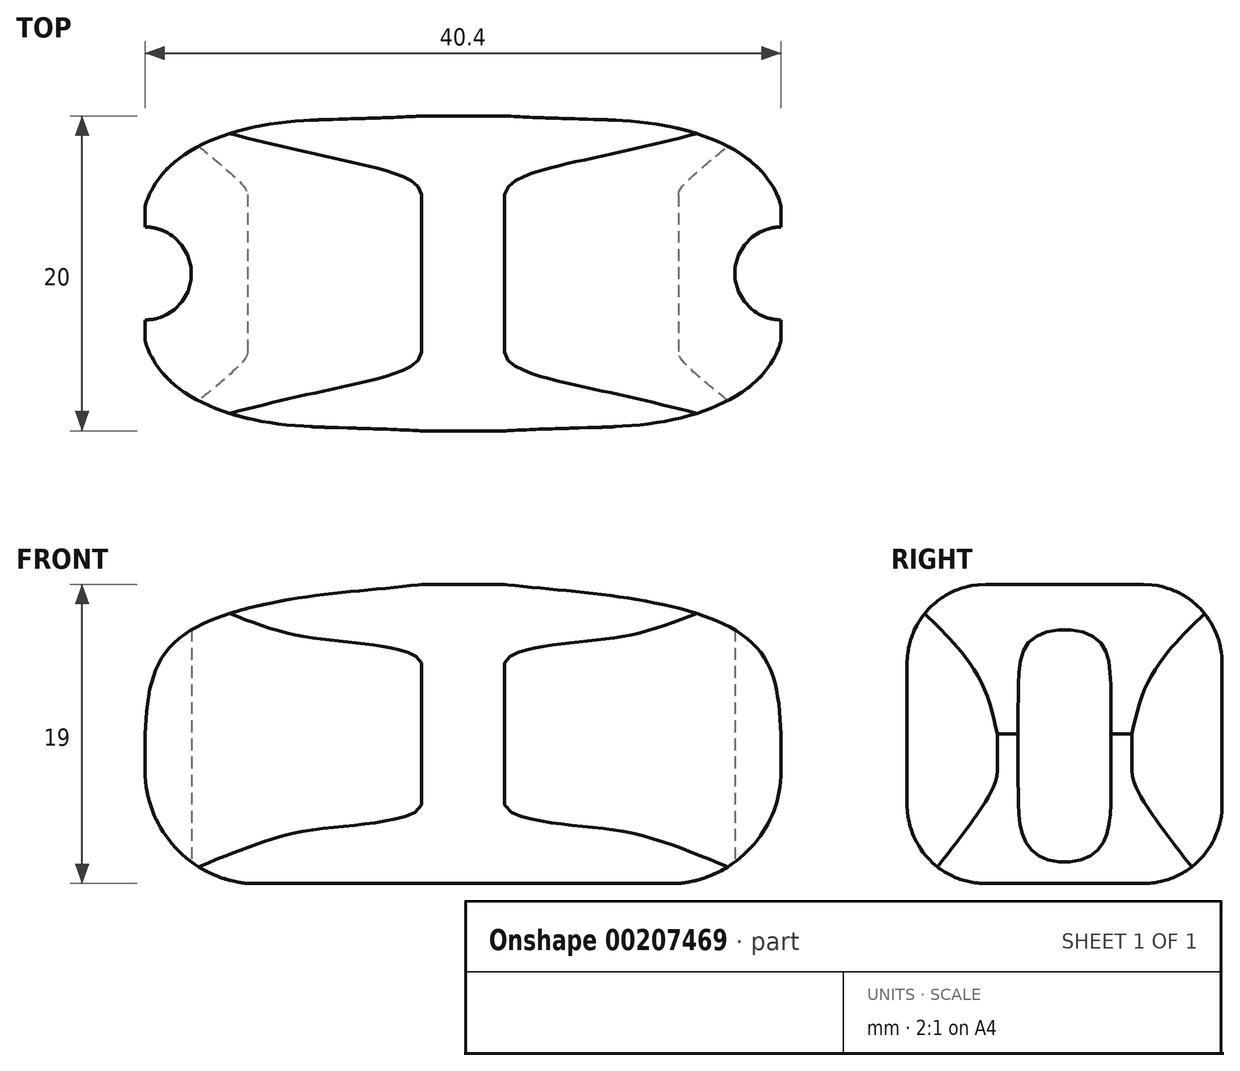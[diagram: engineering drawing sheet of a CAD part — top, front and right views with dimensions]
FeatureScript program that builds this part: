
annotation { "Feature Type Name" : "Feature", "Feature Type Description" : "" }
export const myFeature = defineFeature(function(context is Context, id is Id, definition is map)
    precondition{}
    {
        {
            var Q0;
            Q0=qCreatedBy(makeId("Top.planeOp"),FACE);
            var sketch = newSketch(context, id + "F0", { "sketchPlane" : qUnion([Q0])});
            skLineSegment(sketch, "E0.bottom", {"start": v(-20.2, 10) * mm, "end": v(20.2, 10) * mm});
            skLineSegment(sketch, "E0.top", {"start": v(-20.2, -10) * mm, "end": v(20.2, -10) * mm});
            skLineSegment(sketch, "E0.left", {"start": v(-20.2, 10) * mm, "end": v(-20.2, 2.95) * mm});
            skLineSegment(sketch, "E0.right", {"start": v(20.2, 10) * mm, "end": v(20.2, 2.95) * mm});
            skLineSegment(sketch, "E1", {"start": v(-20.2, 10) * mm, "end": v(20.2, -10) * mm, "construction": true});
            skLineSegment(sketch, "E2", {"start": v(20.2, 10) * mm, "end": v(-20.2, -10) * mm, "construction": true});
            skPoint(sketch, "E3", {"position": v(0, 0) * mm});
            skLineSegment(sketch, "E4", {"start": v(-20.2, 0) * mm, "end": v(20.2, 0) * mm, "construction": true});
            skArc(sketch, "E5", {"start": v(-20.2, -2.95) * mm, "mid": v(-17.25, 0) * mm, "end": v(-20.2, 2.95) * mm});
            skArc(sketch, "E6.MirrorCS", {"start": v(20.2, -2.95) * mm, "mid": v(17.25, 0) * mm, "end": v(20.2, 2.95) * mm});
            skLineSegment(sketch, "E7.trimOffspring", {"start": v(-20.2, -2.95) * mm, "end": v(-20.2, -10) * mm});
            skLineSegment(sketch, "E8.trimOffspring", {"start": v(20.2, -2.95) * mm, "end": v(20.2, -10) * mm});
            skSolve(sketch);
        }
        {
            var Q0;
            Q0 = qSketchRegion(id + "F0", true);
            extrude(context, id + "F1", {"entities" : qUnion([Q0]), "depth" : 19 * mm});
        }
        {
            var Q0;
            Q0=makeQuery(id+"F1.opExtrude","SWEPT_FACE",FACE,{"disambiguationData":[OSD([sQuery(id+"F0.wireOp",EDGE,"E0.top")])]});
            var sketch = newSketch(context, id + "F2", { "sketchPlane" : qUnion([Q0])});
            skFitSpline(sketch, "E9", {"points": [v(-2.64, 19) * mm, v(-10.19, 18.17) * mm, v(-17.3, 16.07) * mm, v(-19.63, 13.32) * mm, v(-20.2, 9.5) * mm], "startDerivative": vector(-19.8, -2.56) * mm, "endDerivative": vector(-1.21, -18.25) * mm});
            skFitSpline(sketch, "E10.MirrorCS", {"points": [v(2.64, 19) * mm, v(10.19, 18.17) * mm, v(17.3, 16.07) * mm, v(19.63, 13.32) * mm, v(20.2, 9.5) * mm], "startDerivative": vector(19.8, -2.56) * mm, "endDerivative": vector(1.21, -18.25) * mm});
            skLineSegment(sketch, "E11", {"start": v(-2.64, 19) * mm, "end": v(2.64, 19) * mm});
            skArc(sketch, "E12", {"start": v(-20.2, 7.18) * mm, "mid": v(-17.83, 1.84) * mm, "end": v(-12.28, 0) * mm});
            skArc(sketch, "E13.MirrorCS", {"start": v(20.2, 7.18) * mm, "mid": v(17.83, 1.84) * mm, "end": v(12.28, 0) * mm});
            skLineSegment(sketch, "E14", {"start": v(-20.2, 9.5) * mm, "end": v(-20.2, 7.18) * mm});
            skLineSegment(sketch, "E15", {"start": v(-12.28, 0) * mm, "end": v(12.28, 0) * mm});
            skLineSegment(sketch, "E16", {"start": v(20.2, 9.5) * mm, "end": v(20.2, 7.18) * mm});
            skSolve(sketch);
        }
        {
            var Q0;
            Q0 = qSketchRegion(id + "F2", true);
            extrude(context, id + "F3", {"entities" : qUnion([Q0]), "operationType" : NewBodyOperationType.INTERSECT, "oppositeDirection" : true, "depth" : 25 * mm});
        }
        {
            var Q0;
            Q0=makeQuery(id+"F1.opExtrude","CAP_FACE",FACE,{"disambiguationData":[OSD([sQuery(id+"F0.wireOp",EDGE,"E0.bottom"),sQuery(id+"F0.wireOp",EDGE,"E0.top"),sQuery(id+"F0.wireOp",EDGE,"E0.left"),sQuery(id+"F0.wireOp",EDGE,"E0.right"),sQuery(id+"F0.wireOp",EDGE,"E5"),sQuery(id+"F0.wireOp",EDGE,"E6.MirrorCS"),sQuery(id+"F0.wireOp",EDGE,"E7.trimOffspring"),sQuery(id+"F0.wireOp",EDGE,"E8.trimOffspring")])],"isStart":false});
            var sketch = newSketch(context, id + "F4", { "sketchPlane" : qUnion([Q0])});
            skFitSpline(sketch, "E17", {"points": [v(-20.24, 4.1) * mm, v(-17.95, 7.38) * mm, v(-12.5, 9.45) * mm, v(-2.64, 10) * mm], "startDerivative": vector(3.5, 14.31) * mm, "endDerivative": vector(33.83, 1.91) * mm});
            skFitSpline(sketch, "E18.MirrorCS", {"points": [v(20.24, 4.1) * mm, v(17.95, 7.38) * mm, v(12.5, 9.45) * mm, v(2.64, 10) * mm], "startDerivative": vector(-3.5, 14.31) * mm, "endDerivative": vector(-33.83, 1.91) * mm});
            skFitSpline(sketch, "E19.MirrorCS", {"points": [v(-20.24, -4.1) * mm, v(-17.95, -7.38) * mm, v(-12.5, -9.45) * mm, v(-2.64, -10) * mm], "startDerivative": vector(3.5, -14.31) * mm, "endDerivative": vector(33.83, -1.91) * mm});
            skFitSpline(sketch, "E20.MirrorCS", {"points": [v(20.24, -4.1) * mm, v(17.95, -7.38) * mm, v(12.5, -9.45) * mm, v(2.64, -10) * mm], "startDerivative": vector(-3.5, -14.31) * mm, "endDerivative": vector(-33.83, -1.91) * mm});
            skLineSegment(sketch, "E21", {"start": v(-2.64, 10) * mm, "end": v(2.64, 10) * mm});
            skLineSegment(sketch, "E22", {"start": v(-2.64, -10) * mm, "end": v(2.64, -10) * mm});
            skLineSegment(sketch, "E23", {"start": v(-20.24, 4.1) * mm, "end": v(-20.24, -4.1) * mm});
            skLineSegment(sketch, "E24", {"start": v(20.24, 4.1) * mm, "end": v(20.24, -4.1) * mm});
            skSolve(sketch);
        }
        {
            var Q0;
            Q0 = qSketchRegion(id + "F4", true);
            extrude(context, id + "F5", {"entities" : qUnion([Q0]), "operationType" : NewBodyOperationType.INTERSECT, "oppositeDirection" : true, "depth" : 25 * mm});
        }
        {
            var Q0;
            Q0=makeQuery(id+"F5.boolean.opBoolean","INTERSECT",EDGE,{"derivedFrom":[makeQuery(id+"F3.boolean.opBoolean","COPY",FACE,{"derivedFrom":makeQuery(id+"F3.boolean.toolComplement.opBoolean","COPY",FACE,{"derivedFrom":makeQuery(id+"F3.opExtrude","SWEPT_FACE",FACE,{"disambiguationData":[OSD([sQuery(id+"F2.wireOp",EDGE,"E9")])]})})}),makeQuery(id+"F5.boolean.toolComplement.opBoolean","COPY",FACE,{"derivedFrom":makeQuery(id+"F5.opExtrude","SWEPT_FACE",FACE,{"disambiguationData":[OSD([sQuery(id+"F4.wireOp",EDGE,"E19.MirrorCS")])]})})]});
            var Q1;
            Q1=makeQuery(id+"F1.opExtrude","CAP_EDGE",EDGE,{"disambiguationData":[OSD([sQuery(id+"F0.wireOp",EDGE,"E0.top")])],"isStart":false});
            var Q2;
            Q2=makeQuery(id+"F5.boolean.opBoolean","INTERSECT",EDGE,{"derivedFrom":[makeQuery(id+"F3.boolean.opBoolean","COPY",FACE,{"derivedFrom":makeQuery(id+"F3.boolean.toolComplement.opBoolean","COPY",FACE,{"derivedFrom":makeQuery(id+"F3.opExtrude","SWEPT_FACE",FACE,{"disambiguationData":[OSD([sQuery(id+"F2.wireOp",EDGE,"E10.MirrorCS")])]})})}),makeQuery(id+"F5.boolean.toolComplement.opBoolean","COPY",FACE,{"derivedFrom":makeQuery(id+"F5.opExtrude","SWEPT_FACE",FACE,{"disambiguationData":[OSD([sQuery(id+"F4.wireOp",EDGE,"E20.MirrorCS")])]})})]});
            var Q3;
            Q3=makeQuery(id+"F5.boolean.opBoolean","INTERSECT",EDGE,{"derivedFrom":[makeQuery(id+"F3.boolean.opBoolean","COPY",FACE,{"derivedFrom":makeQuery(id+"F3.boolean.toolComplement.opBoolean","COPY",FACE,{"derivedFrom":makeQuery(id+"F3.opExtrude","SWEPT_FACE",FACE,{"disambiguationData":[OSD([sQuery(id+"F2.wireOp",EDGE,"E9")])]})})}),makeQuery(id+"F5.boolean.toolComplement.opBoolean","COPY",FACE,{"derivedFrom":makeQuery(id+"F5.opExtrude","SWEPT_FACE",FACE,{"disambiguationData":[OSD([sQuery(id+"F4.wireOp",EDGE,"E17")])]})})]});
            var Q4;
            Q4=makeQuery(id+"F1.opExtrude","CAP_EDGE",EDGE,{"disambiguationData":[OSD([sQuery(id+"F0.wireOp",EDGE,"E0.bottom")])],"isStart":false});
            var Q5;
            Q5=makeQuery(id+"F5.boolean.opBoolean","INTERSECT",EDGE,{"derivedFrom":[makeQuery(id+"F3.boolean.opBoolean","COPY",FACE,{"derivedFrom":makeQuery(id+"F3.boolean.toolComplement.opBoolean","COPY",FACE,{"derivedFrom":makeQuery(id+"F3.opExtrude","SWEPT_FACE",FACE,{"disambiguationData":[OSD([sQuery(id+"F2.wireOp",EDGE,"E10.MirrorCS")])]})})}),makeQuery(id+"F5.boolean.toolComplement.opBoolean","COPY",FACE,{"derivedFrom":makeQuery(id+"F5.opExtrude","SWEPT_FACE",FACE,{"disambiguationData":[OSD([sQuery(id+"F4.wireOp",EDGE,"E18.MirrorCS")])]})})]});
            var Q6;
            Q6=makeQuery(id+"F5.boolean.opBoolean","INTERSECT",EDGE,{"derivedFrom":[makeQuery(id+"F3.boolean.opBoolean","COPY",FACE,{"derivedFrom":makeQuery(id+"F3.boolean.toolComplement.opBoolean","COPY",FACE,{"derivedFrom":makeQuery(id+"F3.opExtrude","SWEPT_FACE",FACE,{"disambiguationData":[OSD([sQuery(id+"F2.wireOp",EDGE,"E12")])]})})}),makeQuery(id+"F5.boolean.toolComplement.opBoolean","COPY",FACE,{"derivedFrom":makeQuery(id+"F5.opExtrude","SWEPT_FACE",FACE,{"disambiguationData":[OSD([sQuery(id+"F4.wireOp",EDGE,"E17")])]})})]});
            var Q7;
            Q7=makeQuery(id+"F5.boolean.opBoolean","INTERSECT",EDGE,{"derivedFrom":[makeQuery(id+"F3.boolean.opBoolean","COPY",FACE,{"derivedFrom":makeQuery(id+"F3.boolean.toolComplement.opBoolean","COPY",FACE,{"derivedFrom":makeQuery(id+"F3.opExtrude","SWEPT_FACE",FACE,{"disambiguationData":[OSD([sQuery(id+"F2.wireOp",EDGE,"E12")])]})})}),makeQuery(id+"F5.boolean.toolComplement.opBoolean","COPY",FACE,{"derivedFrom":makeQuery(id+"F5.opExtrude","SWEPT_FACE",FACE,{"disambiguationData":[OSD([sQuery(id+"F4.wireOp",EDGE,"E19.MirrorCS")])]})})]});
            var Q8;
            Q8=makeQuery(id+"F5.boolean.opBoolean","INTERSECT",EDGE,{"derivedFrom":[makeQuery(id+"F1.opExtrude","CAP_FACE",FACE,{"disambiguationData":[OSD([sQuery(id+"F0.wireOp",EDGE,"E0.bottom"),sQuery(id+"F0.wireOp",EDGE,"E0.top"),sQuery(id+"F0.wireOp",EDGE,"E0.left"),sQuery(id+"F0.wireOp",EDGE,"E0.right"),sQuery(id+"F0.wireOp",EDGE,"E5"),sQuery(id+"F0.wireOp",EDGE,"E6.MirrorCS"),sQuery(id+"F0.wireOp",EDGE,"E7.trimOffspring"),sQuery(id+"F0.wireOp",EDGE,"E8.trimOffspring")])],"isStart":true}),makeQuery(id+"F5.boolean.toolComplement.opBoolean","COPY",FACE,{"derivedFrom":makeQuery(id+"F5.opExtrude","SWEPT_FACE",FACE,{"disambiguationData":[OSD([sQuery(id+"F4.wireOp",EDGE,"E19.MirrorCS")])]})})]});
            var Q9;
            Q9=makeQuery(id+"F5.boolean.opBoolean","INTERSECT",EDGE,{"derivedFrom":[makeQuery(id+"F1.opExtrude","CAP_FACE",FACE,{"disambiguationData":[OSD([sQuery(id+"F0.wireOp",EDGE,"E0.bottom"),sQuery(id+"F0.wireOp",EDGE,"E0.top"),sQuery(id+"F0.wireOp",EDGE,"E0.left"),sQuery(id+"F0.wireOp",EDGE,"E0.right"),sQuery(id+"F0.wireOp",EDGE,"E5"),sQuery(id+"F0.wireOp",EDGE,"E6.MirrorCS"),sQuery(id+"F0.wireOp",EDGE,"E7.trimOffspring"),sQuery(id+"F0.wireOp",EDGE,"E8.trimOffspring")])],"isStart":true}),makeQuery(id+"F5.boolean.toolComplement.opBoolean","COPY",FACE,{"derivedFrom":makeQuery(id+"F5.opExtrude","SWEPT_FACE",FACE,{"disambiguationData":[OSD([sQuery(id+"F4.wireOp",EDGE,"E20.MirrorCS")])]})})]});
            var Q10;
            Q10=makeQuery(id+"F1.opExtrude","CAP_EDGE",EDGE,{"disambiguationData":[OSD([sQuery(id+"F0.wireOp",EDGE,"E0.top")])],"isStart":true});
            var Q11;
            Q11=makeQuery(id+"F5.boolean.opBoolean","INTERSECT",EDGE,{"derivedFrom":[makeQuery(id+"F1.opExtrude","CAP_FACE",FACE,{"disambiguationData":[OSD([sQuery(id+"F0.wireOp",EDGE,"E0.bottom"),sQuery(id+"F0.wireOp",EDGE,"E0.top"),sQuery(id+"F0.wireOp",EDGE,"E0.left"),sQuery(id+"F0.wireOp",EDGE,"E0.right"),sQuery(id+"F0.wireOp",EDGE,"E5"),sQuery(id+"F0.wireOp",EDGE,"E6.MirrorCS"),sQuery(id+"F0.wireOp",EDGE,"E7.trimOffspring"),sQuery(id+"F0.wireOp",EDGE,"E8.trimOffspring")])],"isStart":true}),makeQuery(id+"F5.boolean.toolComplement.opBoolean","COPY",FACE,{"derivedFrom":makeQuery(id+"F5.opExtrude","SWEPT_FACE",FACE,{"disambiguationData":[OSD([sQuery(id+"F4.wireOp",EDGE,"E17")])]})})]});
            var Q12;
            Q12=makeQuery(id+"F1.opExtrude","CAP_EDGE",EDGE,{"disambiguationData":[OSD([sQuery(id+"F0.wireOp",EDGE,"E0.bottom")])],"isStart":true});
            var Q13;
            Q13=makeQuery(id+"F5.boolean.opBoolean","INTERSECT",EDGE,{"derivedFrom":[makeQuery(id+"F1.opExtrude","CAP_FACE",FACE,{"disambiguationData":[OSD([sQuery(id+"F0.wireOp",EDGE,"E0.bottom"),sQuery(id+"F0.wireOp",EDGE,"E0.top"),sQuery(id+"F0.wireOp",EDGE,"E0.left"),sQuery(id+"F0.wireOp",EDGE,"E0.right"),sQuery(id+"F0.wireOp",EDGE,"E5"),sQuery(id+"F0.wireOp",EDGE,"E6.MirrorCS"),sQuery(id+"F0.wireOp",EDGE,"E7.trimOffspring"),sQuery(id+"F0.wireOp",EDGE,"E8.trimOffspring")])],"isStart":true}),makeQuery(id+"F5.boolean.toolComplement.opBoolean","COPY",FACE,{"derivedFrom":makeQuery(id+"F5.opExtrude","SWEPT_FACE",FACE,{"disambiguationData":[OSD([sQuery(id+"F4.wireOp",EDGE,"E18.MirrorCS")])]})})]});
            var Q14;
            Q14=makeQuery(id+"F5.boolean.opBoolean","INTERSECT",EDGE,{"derivedFrom":[makeQuery(id+"F3.boolean.opBoolean","COPY",FACE,{"derivedFrom":makeQuery(id+"F3.boolean.toolComplement.opBoolean","COPY",FACE,{"derivedFrom":makeQuery(id+"F3.opExtrude","SWEPT_FACE",FACE,{"disambiguationData":[OSD([sQuery(id+"F2.wireOp",EDGE,"E13.MirrorCS")])]})})}),makeQuery(id+"F5.boolean.toolComplement.opBoolean","COPY",FACE,{"derivedFrom":makeQuery(id+"F5.opExtrude","SWEPT_FACE",FACE,{"disambiguationData":[OSD([sQuery(id+"F4.wireOp",EDGE,"E18.MirrorCS")])]})})]});
            var Q15;
            Q15=makeQuery(id+"F5.boolean.opBoolean","INTERSECT",EDGE,{"derivedFrom":[makeQuery(id+"F3.boolean.opBoolean","COPY",FACE,{"derivedFrom":makeQuery(id+"F3.boolean.toolComplement.opBoolean","COPY",FACE,{"derivedFrom":makeQuery(id+"F3.opExtrude","SWEPT_FACE",FACE,{"disambiguationData":[OSD([sQuery(id+"F2.wireOp",EDGE,"E13.MirrorCS")])]})})}),makeQuery(id+"F5.boolean.toolComplement.opBoolean","COPY",FACE,{"derivedFrom":makeQuery(id+"F5.opExtrude","SWEPT_FACE",FACE,{"disambiguationData":[OSD([sQuery(id+"F4.wireOp",EDGE,"E20.MirrorCS")])]})})]});
            var Q16;
            Q16=makeQuery(id+"F5.boolean.opBoolean","INTERSECT",EDGE,{"derivedFrom":[makeQuery(id+"F1.opExtrude","SWEPT_FACE",FACE,{"disambiguationData":[OSD([sQuery(id+"F0.wireOp",EDGE,"E8.trimOffspring")])]}),makeQuery(id+"F5.boolean.toolComplement.opBoolean","COPY",FACE,{"derivedFrom":makeQuery(id+"F5.opExtrude","SWEPT_FACE",FACE,{"disambiguationData":[OSD([sQuery(id+"F4.wireOp",EDGE,"E20.MirrorCS")])]})})]});
            var Q17;
            Q17=makeQuery(id+"F5.boolean.opBoolean","INTERSECT",EDGE,{"derivedFrom":[makeQuery(id+"F1.opExtrude","SWEPT_FACE",FACE,{"disambiguationData":[OSD([sQuery(id+"F0.wireOp",EDGE,"E0.right")])]}),makeQuery(id+"F5.boolean.toolComplement.opBoolean","COPY",FACE,{"derivedFrom":makeQuery(id+"F5.opExtrude","SWEPT_FACE",FACE,{"disambiguationData":[OSD([sQuery(id+"F4.wireOp",EDGE,"E18.MirrorCS")])]})})]});
            var Q18;
            Q18=makeQuery(id+"F5.boolean.opBoolean","INTERSECT",EDGE,{"derivedFrom":[makeQuery(id+"F1.opExtrude","SWEPT_FACE",FACE,{"disambiguationData":[OSD([sQuery(id+"F0.wireOp",EDGE,"E7.trimOffspring")])]}),makeQuery(id+"F5.boolean.toolComplement.opBoolean","COPY",FACE,{"derivedFrom":makeQuery(id+"F5.opExtrude","SWEPT_FACE",FACE,{"disambiguationData":[OSD([sQuery(id+"F4.wireOp",EDGE,"E19.MirrorCS")])]})})]});
            var Q19;
            Q19=makeQuery(id+"F5.boolean.opBoolean","INTERSECT",EDGE,{"derivedFrom":[makeQuery(id+"F1.opExtrude","SWEPT_FACE",FACE,{"disambiguationData":[OSD([sQuery(id+"F0.wireOp",EDGE,"E0.left")])]}),makeQuery(id+"F5.boolean.toolComplement.opBoolean","COPY",FACE,{"derivedFrom":makeQuery(id+"F5.opExtrude","SWEPT_FACE",FACE,{"disambiguationData":[OSD([sQuery(id+"F4.wireOp",EDGE,"E17")])]})})]});
            fillet(context, id + "F6", {"entities" : qUnion([Q0, Q1, Q2, Q3, Q4, Q5, Q6, Q7, Q8, Q9, Q10, Q11, Q12, Q13, Q14, Q15, Q16, Q17, Q18, Q19]), "radius" : 5 * mm, "tangentPropagation" : true, "allowEdgeOverflow" : false});
        }
    });
